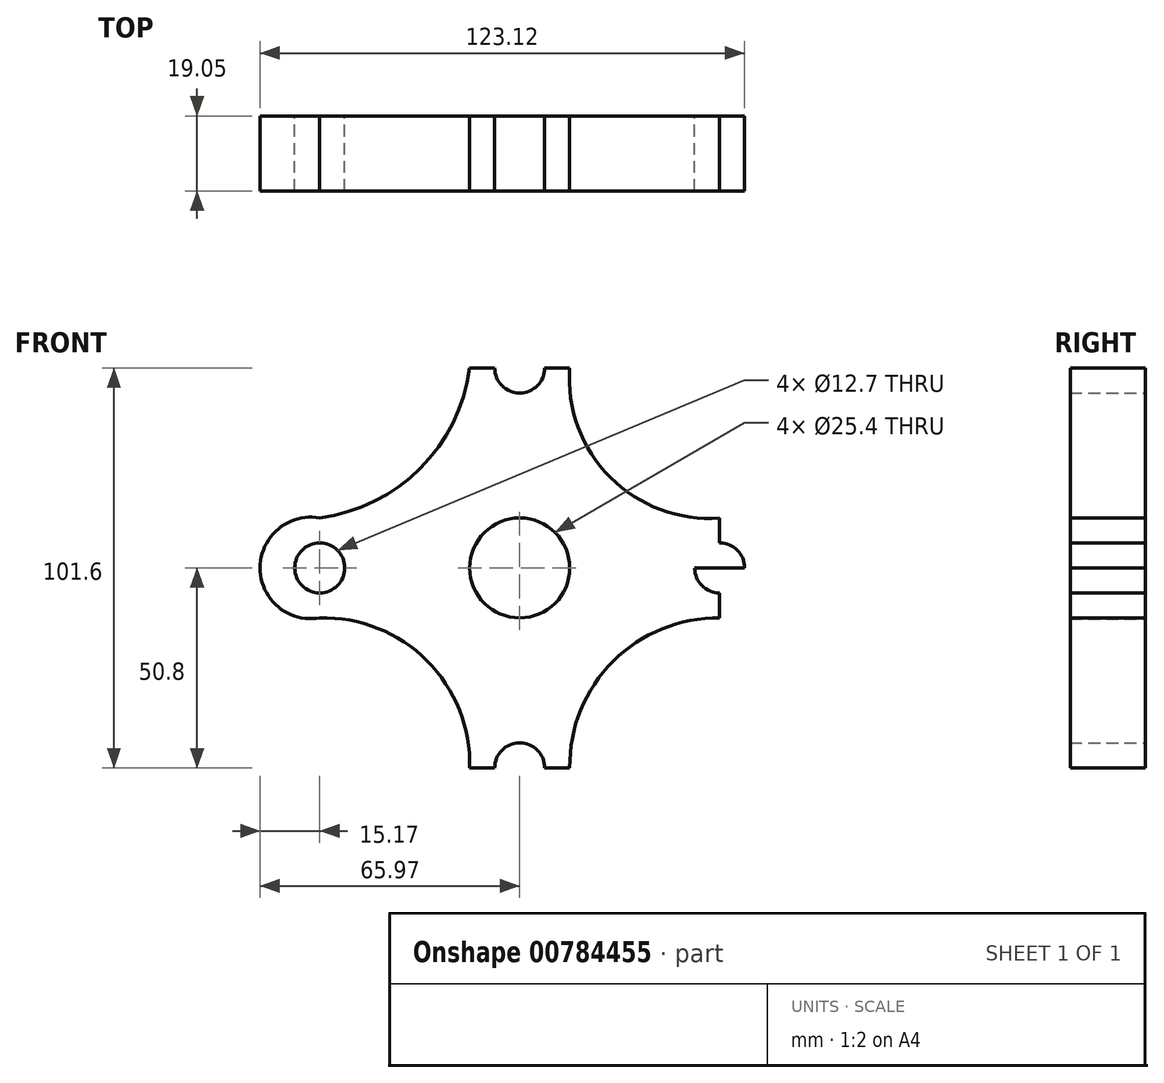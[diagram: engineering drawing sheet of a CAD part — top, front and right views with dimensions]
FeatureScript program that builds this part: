
annotation { "Feature Type Name" : "Feature", "Feature Type Description" : "" }
export const myFeature = defineFeature(function(context is Context, id is Id, definition is map)
    precondition{}
    {
        {
            var Q0;
            Q0=qCreatedBy(makeId("Front.planeOp"),FACE);
            var sketch = newSketch(context, id + "F0", { "sketchPlane" : qUnion([Q0])});
            skCircle(sketch, "E0", {"center": v(0, 0) * mm, "radius": 12.7 * mm});
            skCircle(sketch, "E1", {"center": v(0, 50.8) * mm, "radius": 6.35 * mm});
            skCircle(sketch, "E2.MirrorC", {"center": v(0, -50.8) * mm, "radius": 6.35 * mm});
            skCircle(sketch, "E3", {"center": v(-50.8, 0) * mm, "radius": 6.35 * mm});
            skCircle(sketch, "E4.MirrorC", {"center": v(50.8, 0) * mm, "radius": 6.35 * mm});
            skLineSegment(sketch, "E5", {"start": v(0, 0) * mm, "end": v(0, 71.12) * mm});
            skLineSegment(sketch, "E6", {"start": v(0, 71.12) * mm, "end": v(0, 0) * mm});
            skLineSegment(sketch, "E7", {"start": v(-71.12, 0) * mm, "end": v(0, 0) * mm});
            skLineSegment(sketch, "E8", {"start": v(71.12, 0) * mm, "end": v(0, 0) * mm});
            skLineSegment(sketch, "E9", {"start": v(0, 0) * mm, "end": v(0, -71.12) * mm});
            skLineSegment(sketch, "E10", {"start": v(0, -71.12) * mm, "end": v(0, 0) * mm});
            skLineSegment(sketch, "E11", {"start": v(0, 50.8) * mm, "end": v(-12.7, 50.8) * mm});
            skLineSegment(sketch, "E12", {"start": v(-12.7, 50.8) * mm, "end": v(12.7, 50.8) * mm});
            skLineSegment(sketch, "E13", {"start": v(12.7, 50.8) * mm, "end": v(0, 50.8) * mm});
            skArc(sketch, "E14", {"start": v(12.7, 50.8) * mm, "mid": v(0, 65.48) * mm, "end": v(-12.7, 50.8) * mm});
            skArc(sketch, "E15.MirrorCS", {"start": v(12.7, -50.8) * mm, "mid": v(0, -65.48) * mm, "end": v(-12.7, -50.8) * mm});
            skLineSegment(sketch, "E16.MirrorCS", {"start": v(-12.7, -50.8) * mm, "end": v(12.7, -50.8) * mm});
            skLineSegment(sketch, "E17", {"start": v(-50.8, 0) * mm, "end": v(-50.8, -12.7) * mm});
            skLineSegment(sketch, "E18", {"start": v(-50.8, -12.7) * mm, "end": v(-50.8, 0) * mm});
            skLineSegment(sketch, "E19", {"start": v(-50.8, 12.7) * mm, "end": v(-50.8, 0) * mm});
            skArc(sketch, "E20", {"start": v(-50.8, 12.7) * mm, "mid": v(-65.97, 0) * mm, "end": v(-50.8, -12.7) * mm});
            skArc(sketch, "E21.MirrorCS", {"start": v(50.8, 12.7) * mm, "mid": v(65.97, 0) * mm, "end": v(50.8, -12.7) * mm});
            skLineSegment(sketch, "E22.MirrorCS", {"start": v(50.8, 12.7) * mm, "end": v(50.8, 0) * mm});
            skLineSegment(sketch, "E23.MirrorCS", {"start": v(50.8, -12.7) * mm, "end": v(50.8, 0) * mm});
            skArc(sketch, "E24", {"start": v(12.7, 50.8) * mm, "mid": v(23.02, 23.02) * mm, "end": v(50.8, 12.7) * mm});
            skArc(sketch, "E25", {"start": v(50.8, -12.7) * mm, "mid": v(23.71, -23.71) * mm, "end": v(12.7, -50.8) * mm});
            skArc(sketch, "E26", {"start": v(-12.7, -50.8) * mm, "mid": v(-23.56, -23.56) * mm, "end": v(-50.8, -12.7) * mm});
            skArc(sketch, "E27", {"start": v(-50.8, 12.7) * mm, "mid": v(-25.3, 25.3) * mm, "end": v(-12.7, 50.8) * mm});
            skSolve(sketch);
        }
        {
            var Q0;
            {var subQ11=sQuery(id+"F0.wireOp",EDGE,"E27");Q0=makeQuery(id+"F0.imprint","IMPRINT",FACE,{"disambiguationData":[TD([[makeQuery(id+"F0.imprint","IMPRINT",EDGE,{"derivedFrom":subQ11}),-1.0]])]});}
            var Q1;
            {var subQ10=sQuery(id+"F0.wireOp",EDGE,"E24");Q1=makeQuery(id+"F0.imprint","IMPRINT",FACE,{"disambiguationData":[TD([[makeQuery(id+"F0.imprint","IMPRINT",EDGE,{"derivedFrom":subQ10}),-1.0]])]});}
            var Q2;
            {var subQ0=sQuery(id+"F0.wireOp",EDGE,"E6");var subQ1=sQuery(id+"F0.wireOp",EDGE,"E1");var subQ2=makeQuery(id+"F0.imprint","INTERSECT",VERTEX,{"disambiguationData":[OD(0.0)],"derivedFrom":[subQ1,subQ0]});Q2=makeQuery(id+"F0.imprint","IMPRINT",FACE,{"disambiguationData":[TD([[makeQuery(id+"F0.imprint","IMPRINT",EDGE,{"disambiguationData":[TD([[subQ2,1.0]])],"derivedFrom":subQ1}),-1.0]])]});}
            var Q3;
            {var subQ0=sQuery(id+"F0.wireOp",EDGE,"E6");var subQ1=sQuery(id+"F0.wireOp",EDGE,"E1");var subQ2=makeQuery(id+"F0.imprint","INTERSECT",VERTEX,{"disambiguationData":[OD(0.0)],"derivedFrom":[subQ1,subQ0]});Q3=makeQuery(id+"F0.imprint","IMPRINT",FACE,{"disambiguationData":[TD([[makeQuery(id+"F0.imprint","IMPRINT",EDGE,{"disambiguationData":[TD([[subQ2,-1.0]])],"derivedFrom":subQ1}),-1.0]])]});}
            var Q4;
            {var subQ0=sQuery(id+"F0.wireOp",EDGE,"E19");var subQ1=sQuery(id+"F0.wireOp",EDGE,"E3");var subQ2=makeQuery(id+"F0.imprint","INTERSECT",VERTEX,{"derivedFrom":[subQ1,subQ0]});Q4=makeQuery(id+"F0.imprint","IMPRINT",FACE,{"disambiguationData":[TD([[makeQuery(id+"F0.imprint","IMPRINT",EDGE,{"disambiguationData":[TD([[subQ2,-1.0]])],"derivedFrom":subQ1}),-1.0]])]});}
            var Q5;
            {var subQ0=sQuery(id+"F0.wireOp",EDGE,"E7");var subQ1=sQuery(id+"F0.wireOp",EDGE,"E3");var subQ2=makeQuery(id+"F0.imprint","INTERSECT",VERTEX,{"disambiguationData":[OD(1.0)],"derivedFrom":[subQ1,subQ0]});Q5=makeQuery(id+"F0.imprint","IMPRINT",FACE,{"disambiguationData":[TD([[makeQuery(id+"F0.imprint","IMPRINT",EDGE,{"disambiguationData":[TD([[subQ2,-1.0]])],"derivedFrom":subQ1}),-1.0]])]});}
            var Q6;
            {var subQ7=sQuery(id+"F0.wireOp",EDGE,"E26");Q6=makeQuery(id+"F0.imprint","IMPRINT",FACE,{"disambiguationData":[TD([[makeQuery(id+"F0.imprint","IMPRINT",EDGE,{"derivedFrom":subQ7}),-1.0]])]});}
            var Q7;
            {var subQ13=sQuery(id+"F0.wireOp",EDGE,"E25");Q7=makeQuery(id+"F0.imprint","IMPRINT",FACE,{"disambiguationData":[TD([[makeQuery(id+"F0.imprint","IMPRINT",EDGE,{"derivedFrom":subQ13}),-1.0]])]});}
            var Q8;
            {var subQ0=sQuery(id+"F0.wireOp",EDGE,"E8");var subQ1=sQuery(id+"F0.wireOp",EDGE,"E4.MirrorC");var subQ2=makeQuery(id+"F0.imprint","INTERSECT",VERTEX,{"disambiguationData":[OD(1.0)],"derivedFrom":[subQ1,subQ0]});Q8=makeQuery(id+"F0.imprint","IMPRINT",FACE,{"disambiguationData":[TD([[makeQuery(id+"F0.imprint","IMPRINT",EDGE,{"disambiguationData":[TD([[subQ2,-1.0]])],"derivedFrom":subQ1}),1.0]])]});}
            var Q9;
            {var subQ0=sQuery(id+"F0.wireOp",EDGE,"E10");var subQ1=sQuery(id+"F0.wireOp",EDGE,"E2.MirrorC");var subQ2=makeQuery(id+"F0.imprint","INTERSECT",VERTEX,{"disambiguationData":[OD(0.0)],"derivedFrom":[subQ1,subQ0]});Q9=makeQuery(id+"F0.imprint","IMPRINT",FACE,{"disambiguationData":[TD([[makeQuery(id+"F0.imprint","IMPRINT",EDGE,{"disambiguationData":[TD([[subQ2,1.0]])],"derivedFrom":subQ1}),1.0]])]});}
            var Q10;
            {var subQ0=sQuery(id+"F0.wireOp",EDGE,"E10");var subQ1=sQuery(id+"F0.wireOp",EDGE,"E2.MirrorC");var subQ2=makeQuery(id+"F0.imprint","INTERSECT",VERTEX,{"disambiguationData":[OD(0.0)],"derivedFrom":[subQ1,subQ0]});Q10=makeQuery(id+"F0.imprint","IMPRINT",FACE,{"disambiguationData":[TD([[makeQuery(id+"F0.imprint","IMPRINT",EDGE,{"disambiguationData":[TD([[subQ2,-1.0]])],"derivedFrom":subQ1}),1.0]])]});}
            var Q11;
            {var subQ0=sQuery(id+"F0.wireOp",EDGE,"E22.MirrorCS");var subQ1=sQuery(id+"F0.wireOp",EDGE,"E4.MirrorC");var subQ2=makeQuery(id+"F0.imprint","INTERSECT",VERTEX,{"derivedFrom":[subQ1,subQ0]});Q11=makeQuery(id+"F0.imprint","IMPRINT",FACE,{"disambiguationData":[TD([[makeQuery(id+"F0.imprint","IMPRINT",EDGE,{"disambiguationData":[TD([[subQ2,-1.0]])],"derivedFrom":subQ1}),1.0]])]});}
            extrude(context, id + "F1", {"entities" : qUnion([Q0, Q1, Q2, Q3, Q4, Q5, Q6, Q7, Q8, Q9, Q10, Q11]), "depth" : 19.05 * mm, "offsetDistance" : 25.4 * mm});
        }
    });
